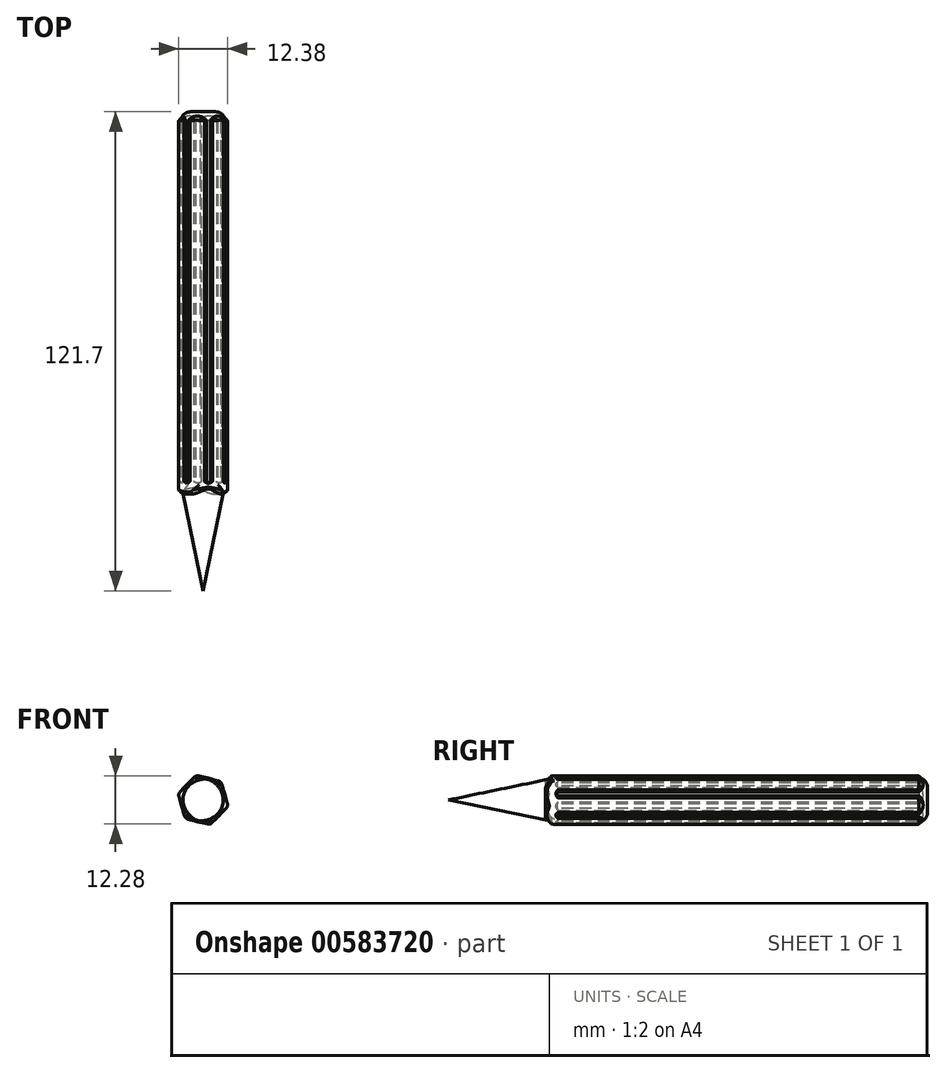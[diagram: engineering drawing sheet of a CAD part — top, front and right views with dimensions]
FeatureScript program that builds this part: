
annotation { "Feature Type Name" : "Feature", "Feature Type Description" : "" }
export const myFeature = defineFeature(function(context is Context, id is Id, definition is map)
    precondition{}
    {
        {
            var Q0;
            Q0=qCreatedBy(makeId("Right.planeOp"),FACE);
            var sketch = newSketch(context, id + "F0", { "sketchPlane" : qUnion([Q0])});
            skLineSegment(sketch, "E0.bottom", {"start": v(-45.04, 0) * mm, "end": v(49.08, 0) * mm});
            skLineSegment(sketch, "E0.top", {"start": v(-45.04, 5.71) * mm, "end": v(49.08, 5.71) * mm});
            skLineSegment(sketch, "E0.left", {"start": v(-45.04, 0) * mm, "end": v(-45.04, 5.71) * mm});
            skLineSegment(sketch, "E0.right", {"start": v(49.08, 0) * mm, "end": v(49.08, 5.71) * mm});
            skLineSegment(sketch, "E1", {"start": v(-45.04, 5.71) * mm, "end": v(-72.62, 0) * mm});
            skLineSegment(sketch, "E2", {"start": v(-72.62, 0) * mm, "end": v(-45.04, 0) * mm});
            skSolve(sketch);
        }
        {
            var Q0;
            Q0=qCreatedBy(makeId("Right.planeOp"),FACE);
            var sketch = newSketch(context, id + "F1", { "sketchPlane" : qUnion([Q0])});
            skSolve(sketch);
        }
        {
            var Q0;
            Q0 = qSketchRegion(id + "F1", true);
            var Q1;
            Q1=makeQuery(id+"F0.imprint","IMPRINT",FACE,{"disambiguationData":[TD([[makeQuery(id+"F0.imprint","IMPRINT",EDGE,{"derivedFrom":sQuery(id+"F0.wireOp",EDGE,"E0.left")}),1.0]])]});
            var Q2;
            Q2=makeQuery(id+"F0.imprint","IMPRINT",FACE,{"disambiguationData":[TD([[makeQuery(id+"F0.imprint","IMPRINT",EDGE,{"derivedFrom":sQuery(id+"F0.wireOp",EDGE,"E0.bottom")}),1.0]])]});
            var Q3;
            Q3=sQuery(id+"F0.wireOp",EDGE,"E0.bottom");
            revolve(context, id + "F2", {"entities" : qUnion([Q0, Q1, Q2]), "axis" : qUnion([Q3]), "revolveType" : RevolveType.FULL});
        }
        {
            var Q0;
            Q0=qCreatedBy(makeId("Front.planeOp"),FACE);
            var sketch = newSketch(context, id + "F3", { "sketchPlane" : qUnion([Q0])});
            skCircle(sketch, "E3.cCircle", {"center": v(0, 0) * mm, "radius": 5.66 * mm, "construction": true});
            skLineSegment(sketch, "E3.0", {"start": v(-4.53, -4.71) * mm, "end": v(-6.35, 1.57) * mm});
            skLineSegment(sketch, "E3.1", {"start": v(-6.35, 1.57) * mm, "end": v(-1.81, 6.28) * mm});
            skLineSegment(sketch, "E3.2", {"start": v(-1.81, 6.28) * mm, "end": v(4.53, 4.71) * mm});
            skLineSegment(sketch, "E3.3", {"start": v(4.53, 4.71) * mm, "end": v(6.35, -1.57) * mm});
            skLineSegment(sketch, "E3.4", {"start": v(6.35, -1.57) * mm, "end": v(1.81, -6.28) * mm});
            skLineSegment(sketch, "E3.5", {"start": v(1.81, -6.28) * mm, "end": v(-4.53, -4.71) * mm});
            skPoint(sketch, "E3.0.midPoint", {"position": v(-5.44, -1.57) * mm});
            skSolve(sketch);
        }
        {
            var Q0;
            Q0 = qSketchRegion(id + "F3", true);
            extrude(context, id + "F4", {"entities" : qUnion([Q0]), "operationType" : NewBodyOperationType.ADD, "endBound" : BoundingType.SYMMETRIC, "depth" : 93.98 * mm, "offsetDistance" : 25.4 * mm});
        }
        {
            var Q0;
            Q0=makeQuery(id+"F4.opExtrude","SWEPT_EDGE",EDGE,{"disambiguationData":[OSD([sQuery(id+"F3.wireOp",EDGE,"E3.3"),sQuery(id+"F3.wireOp",EDGE,"E3.4")])]});
            var Q1;
            Q1=makeQuery(id+"F4.opExtrude","SWEPT_EDGE",EDGE,{"disambiguationData":[OSD([sQuery(id+"F3.wireOp",EDGE,"E3.2"),sQuery(id+"F3.wireOp",EDGE,"E3.3")])]});
            var Q2;
            Q2=makeQuery(id+"F4.opExtrude","SWEPT_EDGE",EDGE,{"disambiguationData":[OSD([sQuery(id+"F3.wireOp",EDGE,"E3.1"),sQuery(id+"F3.wireOp",EDGE,"E3.2")])]});
            var Q3;
            Q3=makeQuery(id+"F4.opExtrude","SWEPT_EDGE",EDGE,{"disambiguationData":[OSD([sQuery(id+"F3.wireOp",EDGE,"E3.0"),sQuery(id+"F3.wireOp",EDGE,"E3.1")])]});
            var Q4;
            Q4=makeQuery(id+"F4.opExtrude","SWEPT_EDGE",EDGE,{"disambiguationData":[OSD([sQuery(id+"F3.wireOp",EDGE,"E3.0"),sQuery(id+"F3.wireOp",EDGE,"E3.5")])]});
            var Q5;
            Q5=makeQuery(id+"F4.opExtrude","SWEPT_EDGE",EDGE,{"disambiguationData":[OSD([sQuery(id+"F3.wireOp",EDGE,"E3.4"),sQuery(id+"F3.wireOp",EDGE,"E3.5")])]});
            var Q6;
            Q6=makeQuery(id+"F4.opExtrude","CAP_EDGE",EDGE,{"disambiguationData":[OSD([sQuery(id+"F3.wireOp",EDGE,"E3.5")])],"isStart":false});
            var Q7;
            Q7=makeQuery(id+"F4.opExtrude","CAP_EDGE",EDGE,{"disambiguationData":[OSD([sQuery(id+"F3.wireOp",EDGE,"E3.2")])],"isStart":false});
            fillet(context, id + "F5", {"entities" : qUnion([Q0, Q1, Q2, Q3, Q4, Q5, Q6, Q7]), "radius" : 1.27 * mm, "tangentPropagation" : true, "allowEdgeOverflow" : false});
        }
        {
            var Q0;
            Q0=makeQuery(id+"F2.opRevolve","SWEPT_EDGE",EDGE,{"disambiguationData":[OSD([sQuery(id+"F0.wireOp",EDGE,"E0.top"),sQuery(id+"F0.wireOp",EDGE,"E0.right")])]});
            fillet(context, id + "F6", {"entities" : qUnion([Q0]), "radius" : 2.54 * mm, "tangentPropagation" : true, "allowEdgeOverflow" : false});
        }
        {
            var Q0;
            {var subQ0=sQuery(id+"F3.wireOp",EDGE,"E3.0");var subQ1=sQuery(id+"F3.wireOp",EDGE,"E3.1");Q0=makeQuery(id+"F5.opFillet","BLEND_EDGE",EDGE,{"blendedFrom":[makeQuery(id+"F4.opExtrude","SWEPT_EDGE",EDGE,{"disambiguationData":[OSD([subQ0,subQ1])]}),makeQuery(id+"F4.boolean.opBoolean","SPLIT",FACE,{"disambiguationData":[TD([makeQuery(id+"F2.opRevolve","SWEPT_FACE",FACE,{"disambiguationData":[OSD([sQuery(id+"F0.wireOp",EDGE,"E0.top")])]}),makeQuery(id+"F4.opExtrude","SWEPT_FACE",FACE,{"disambiguationData":[OSD([subQ0])]}),makeQuery(id+"F4.opExtrude","SWEPT_FACE",FACE,{"disambiguationData":[OSD([subQ1])]})])],"derivedFrom":makeQuery(id+"F4.opExtrude","CAP_FACE",FACE,{"disambiguationData":[OSD([subQ0,subQ1,sQuery(id+"F3.wireOp",EDGE,"E3.2"),sQuery(id+"F3.wireOp",EDGE,"E3.3"),sQuery(id+"F3.wireOp",EDGE,"E3.4"),sQuery(id+"F3.wireOp",EDGE,"E3.5")])],"isStart":true})})],"blendedInto":[makeQuery(id+"F4.boolean.opBoolean","SPLIT",FACE,{"disambiguationData":[TD([makeQuery(id+"F2.opRevolve","SWEPT_FACE",FACE,{"disambiguationData":[OSD([sQuery(id+"F0.wireOp",EDGE,"E0.top")])]}),makeQuery(id+"F4.opExtrude","SWEPT_FACE",FACE,{"disambiguationData":[OSD([subQ0])]}),makeQuery(id+"F4.opExtrude","SWEPT_FACE",FACE,{"disambiguationData":[OSD([subQ1])]})])],"derivedFrom":makeQuery(id+"F4.opExtrude","CAP_FACE",FACE,{"disambiguationData":[OSD([subQ0,subQ1,sQuery(id+"F3.wireOp",EDGE,"E3.2"),sQuery(id+"F3.wireOp",EDGE,"E3.3"),sQuery(id+"F3.wireOp",EDGE,"E3.4"),sQuery(id+"F3.wireOp",EDGE,"E3.5")])],"isStart":true})})]});}
            var Q1;
            {var subQ0=sQuery(id+"F3.wireOp",EDGE,"E3.0");var subQ1=sQuery(id+"F3.wireOp",EDGE,"E3.1");Q1=makeQuery(id+"F4.boolean.opBoolean","SPLIT",EDGE,{"disambiguationData":[TD([makeQuery(id+"F4.opExtrude","SWEPT_FACE",FACE,{"disambiguationData":[OSD([subQ1])]})])],"derivedFrom":makeQuery(id+"F4.opExtrude","CAP_EDGE",EDGE,{"disambiguationData":[OSD([subQ0])],"isStart":true})});}
            var Q2;
            {var subQ0=sQuery(id+"F3.wireOp",EDGE,"E3.0");var subQ1=sQuery(id+"F3.wireOp",EDGE,"E3.1");Q2=makeQuery(id+"F4.boolean.opBoolean","SPLIT",EDGE,{"disambiguationData":[TD([makeQuery(id+"F4.opExtrude","SWEPT_FACE",FACE,{"disambiguationData":[OSD([subQ0])]})])],"derivedFrom":makeQuery(id+"F4.opExtrude","CAP_EDGE",EDGE,{"disambiguationData":[OSD([subQ1])],"isStart":true})});}
            var Q3;
            {var subQ0=sQuery(id+"F3.wireOp",EDGE,"E3.2");var subQ1=sQuery(id+"F3.wireOp",EDGE,"E3.1");Q3=makeQuery(id+"F4.boolean.opBoolean","SPLIT",EDGE,{"disambiguationData":[TD([makeQuery(id+"F4.opExtrude","SWEPT_FACE",FACE,{"disambiguationData":[OSD([subQ0])]})])],"derivedFrom":makeQuery(id+"F4.opExtrude","CAP_EDGE",EDGE,{"disambiguationData":[OSD([subQ1])],"isStart":true})});}
            var Q4;
            {var subQ0=sQuery(id+"F3.wireOp",EDGE,"E3.1");var subQ1=sQuery(id+"F3.wireOp",EDGE,"E3.2");Q4=makeQuery(id+"F5.opFillet","BLEND_EDGE",EDGE,{"blendedFrom":[makeQuery(id+"F4.opExtrude","SWEPT_EDGE",EDGE,{"disambiguationData":[OSD([subQ0,subQ1])]}),makeQuery(id+"F4.boolean.opBoolean","SPLIT",FACE,{"disambiguationData":[TD([makeQuery(id+"F2.opRevolve","SWEPT_FACE",FACE,{"disambiguationData":[OSD([sQuery(id+"F0.wireOp",EDGE,"E0.top")])]}),makeQuery(id+"F4.opExtrude","SWEPT_FACE",FACE,{"disambiguationData":[OSD([subQ0])]}),makeQuery(id+"F4.opExtrude","SWEPT_FACE",FACE,{"disambiguationData":[OSD([subQ1])]})])],"derivedFrom":makeQuery(id+"F4.opExtrude","CAP_FACE",FACE,{"disambiguationData":[OSD([sQuery(id+"F3.wireOp",EDGE,"E3.0"),subQ0,subQ1,sQuery(id+"F3.wireOp",EDGE,"E3.3"),sQuery(id+"F3.wireOp",EDGE,"E3.4"),sQuery(id+"F3.wireOp",EDGE,"E3.5")])],"isStart":true})})],"blendedInto":[makeQuery(id+"F4.boolean.opBoolean","SPLIT",FACE,{"disambiguationData":[TD([makeQuery(id+"F2.opRevolve","SWEPT_FACE",FACE,{"disambiguationData":[OSD([sQuery(id+"F0.wireOp",EDGE,"E0.top")])]}),makeQuery(id+"F4.opExtrude","SWEPT_FACE",FACE,{"disambiguationData":[OSD([subQ0])]}),makeQuery(id+"F4.opExtrude","SWEPT_FACE",FACE,{"disambiguationData":[OSD([subQ1])]})])],"derivedFrom":makeQuery(id+"F4.opExtrude","CAP_FACE",FACE,{"disambiguationData":[OSD([sQuery(id+"F3.wireOp",EDGE,"E3.0"),subQ0,subQ1,sQuery(id+"F3.wireOp",EDGE,"E3.3"),sQuery(id+"F3.wireOp",EDGE,"E3.4"),sQuery(id+"F3.wireOp",EDGE,"E3.5")])],"isStart":true})})]});}
            var Q5;
            {var subQ0=sQuery(id+"F3.wireOp",EDGE,"E3.2");var subQ1=sQuery(id+"F3.wireOp",EDGE,"E3.1");Q5=makeQuery(id+"F4.boolean.opBoolean","SPLIT",EDGE,{"disambiguationData":[TD([makeQuery(id+"F4.opExtrude","SWEPT_FACE",FACE,{"disambiguationData":[OSD([subQ1])]})])],"derivedFrom":makeQuery(id+"F4.opExtrude","CAP_EDGE",EDGE,{"disambiguationData":[OSD([subQ0])],"isStart":true})});}
            var Q6;
            {var subQ0=sQuery(id+"F3.wireOp",EDGE,"E3.3");var subQ1=sQuery(id+"F3.wireOp",EDGE,"E3.2");Q6=makeQuery(id+"F4.boolean.opBoolean","SPLIT",EDGE,{"disambiguationData":[TD([makeQuery(id+"F4.opExtrude","SWEPT_FACE",FACE,{"disambiguationData":[OSD([subQ0])]})])],"derivedFrom":makeQuery(id+"F4.opExtrude","CAP_EDGE",EDGE,{"disambiguationData":[OSD([subQ1])],"isStart":true})});}
            var Q7;
            {var subQ0=sQuery(id+"F3.wireOp",EDGE,"E3.3");var subQ1=sQuery(id+"F3.wireOp",EDGE,"E3.2");Q7=makeQuery(id+"F5.opFillet","BLEND_EDGE",EDGE,{"blendedFrom":[makeQuery(id+"F4.opExtrude","SWEPT_EDGE",EDGE,{"disambiguationData":[OSD([subQ1,subQ0])]}),makeQuery(id+"F4.boolean.opBoolean","SPLIT",FACE,{"disambiguationData":[TD([makeQuery(id+"F2.opRevolve","SWEPT_FACE",FACE,{"disambiguationData":[OSD([sQuery(id+"F0.wireOp",EDGE,"E0.top")])]}),makeQuery(id+"F4.opExtrude","SWEPT_FACE",FACE,{"disambiguationData":[OSD([subQ1])]}),makeQuery(id+"F4.opExtrude","SWEPT_FACE",FACE,{"disambiguationData":[OSD([subQ0])]})])],"derivedFrom":makeQuery(id+"F4.opExtrude","CAP_FACE",FACE,{"disambiguationData":[OSD([sQuery(id+"F3.wireOp",EDGE,"E3.0"),sQuery(id+"F3.wireOp",EDGE,"E3.1"),subQ1,subQ0,sQuery(id+"F3.wireOp",EDGE,"E3.4"),sQuery(id+"F3.wireOp",EDGE,"E3.5")])],"isStart":true})})],"blendedInto":[makeQuery(id+"F4.boolean.opBoolean","SPLIT",FACE,{"disambiguationData":[TD([makeQuery(id+"F2.opRevolve","SWEPT_FACE",FACE,{"disambiguationData":[OSD([sQuery(id+"F0.wireOp",EDGE,"E0.top")])]}),makeQuery(id+"F4.opExtrude","SWEPT_FACE",FACE,{"disambiguationData":[OSD([subQ1])]}),makeQuery(id+"F4.opExtrude","SWEPT_FACE",FACE,{"disambiguationData":[OSD([subQ0])]})])],"derivedFrom":makeQuery(id+"F4.opExtrude","CAP_FACE",FACE,{"disambiguationData":[OSD([sQuery(id+"F3.wireOp",EDGE,"E3.0"),sQuery(id+"F3.wireOp",EDGE,"E3.1"),subQ1,subQ0,sQuery(id+"F3.wireOp",EDGE,"E3.4"),sQuery(id+"F3.wireOp",EDGE,"E3.5")])],"isStart":true})})]});}
            var Q8;
            {var subQ0=sQuery(id+"F3.wireOp",EDGE,"E3.3");var subQ1=sQuery(id+"F3.wireOp",EDGE,"E3.2");Q8=makeQuery(id+"F4.boolean.opBoolean","SPLIT",EDGE,{"disambiguationData":[TD([makeQuery(id+"F4.opExtrude","SWEPT_FACE",FACE,{"disambiguationData":[OSD([subQ1])]})])],"derivedFrom":makeQuery(id+"F4.opExtrude","CAP_EDGE",EDGE,{"disambiguationData":[OSD([subQ0])],"isStart":true})});}
            var Q9;
            {var subQ0=sQuery(id+"F3.wireOp",EDGE,"E3.3");var subQ1=sQuery(id+"F3.wireOp",EDGE,"E3.4");Q9=makeQuery(id+"F4.boolean.opBoolean","SPLIT",EDGE,{"disambiguationData":[TD([makeQuery(id+"F4.opExtrude","SWEPT_FACE",FACE,{"disambiguationData":[OSD([subQ1])]})])],"derivedFrom":makeQuery(id+"F4.opExtrude","CAP_EDGE",EDGE,{"disambiguationData":[OSD([subQ0])],"isStart":true})});}
            var Q10;
            {var subQ0=sQuery(id+"F3.wireOp",EDGE,"E3.3");var subQ1=sQuery(id+"F3.wireOp",EDGE,"E3.4");Q10=makeQuery(id+"F5.opFillet","BLEND_EDGE",EDGE,{"blendedFrom":[makeQuery(id+"F4.opExtrude","SWEPT_EDGE",EDGE,{"disambiguationData":[OSD([subQ0,subQ1])]}),makeQuery(id+"F4.boolean.opBoolean","SPLIT",FACE,{"disambiguationData":[TD([makeQuery(id+"F2.opRevolve","SWEPT_FACE",FACE,{"disambiguationData":[OSD([sQuery(id+"F0.wireOp",EDGE,"E0.top")])]}),makeQuery(id+"F4.opExtrude","SWEPT_FACE",FACE,{"disambiguationData":[OSD([subQ0])]}),makeQuery(id+"F4.opExtrude","SWEPT_FACE",FACE,{"disambiguationData":[OSD([subQ1])]})])],"derivedFrom":makeQuery(id+"F4.opExtrude","CAP_FACE",FACE,{"disambiguationData":[OSD([sQuery(id+"F3.wireOp",EDGE,"E3.0"),sQuery(id+"F3.wireOp",EDGE,"E3.1"),sQuery(id+"F3.wireOp",EDGE,"E3.2"),subQ0,subQ1,sQuery(id+"F3.wireOp",EDGE,"E3.5")])],"isStart":true})})],"blendedInto":[makeQuery(id+"F4.boolean.opBoolean","SPLIT",FACE,{"disambiguationData":[TD([makeQuery(id+"F2.opRevolve","SWEPT_FACE",FACE,{"disambiguationData":[OSD([sQuery(id+"F0.wireOp",EDGE,"E0.top")])]}),makeQuery(id+"F4.opExtrude","SWEPT_FACE",FACE,{"disambiguationData":[OSD([subQ0])]}),makeQuery(id+"F4.opExtrude","SWEPT_FACE",FACE,{"disambiguationData":[OSD([subQ1])]})])],"derivedFrom":makeQuery(id+"F4.opExtrude","CAP_FACE",FACE,{"disambiguationData":[OSD([sQuery(id+"F3.wireOp",EDGE,"E3.0"),sQuery(id+"F3.wireOp",EDGE,"E3.1"),sQuery(id+"F3.wireOp",EDGE,"E3.2"),subQ0,subQ1,sQuery(id+"F3.wireOp",EDGE,"E3.5")])],"isStart":true})})]});}
            var Q11;
            {var subQ0=sQuery(id+"F3.wireOp",EDGE,"E3.3");var subQ1=sQuery(id+"F3.wireOp",EDGE,"E3.4");Q11=makeQuery(id+"F4.boolean.opBoolean","SPLIT",EDGE,{"disambiguationData":[TD([makeQuery(id+"F4.opExtrude","SWEPT_FACE",FACE,{"disambiguationData":[OSD([subQ0])]})])],"derivedFrom":makeQuery(id+"F4.opExtrude","CAP_EDGE",EDGE,{"disambiguationData":[OSD([subQ1])],"isStart":true})});}
            var Q12;
            {var subQ0=sQuery(id+"F3.wireOp",EDGE,"E3.5");var subQ1=sQuery(id+"F3.wireOp",EDGE,"E3.4");Q12=makeQuery(id+"F4.boolean.opBoolean","SPLIT",EDGE,{"disambiguationData":[TD([makeQuery(id+"F4.opExtrude","SWEPT_FACE",FACE,{"disambiguationData":[OSD([subQ0])]})])],"derivedFrom":makeQuery(id+"F4.opExtrude","CAP_EDGE",EDGE,{"disambiguationData":[OSD([subQ1])],"isStart":true})});}
            var Q13;
            {var subQ0=sQuery(id+"F3.wireOp",EDGE,"E3.4");var subQ1=sQuery(id+"F3.wireOp",EDGE,"E3.5");Q13=makeQuery(id+"F5.opFillet","BLEND_EDGE",EDGE,{"blendedFrom":[makeQuery(id+"F4.opExtrude","SWEPT_EDGE",EDGE,{"disambiguationData":[OSD([subQ0,subQ1])]}),makeQuery(id+"F4.boolean.opBoolean","SPLIT",FACE,{"disambiguationData":[TD([makeQuery(id+"F2.opRevolve","SWEPT_FACE",FACE,{"disambiguationData":[OSD([sQuery(id+"F0.wireOp",EDGE,"E0.top")])]}),makeQuery(id+"F4.opExtrude","SWEPT_FACE",FACE,{"disambiguationData":[OSD([subQ0])]}),makeQuery(id+"F4.opExtrude","SWEPT_FACE",FACE,{"disambiguationData":[OSD([subQ1])]})])],"derivedFrom":makeQuery(id+"F4.opExtrude","CAP_FACE",FACE,{"disambiguationData":[OSD([sQuery(id+"F3.wireOp",EDGE,"E3.0"),sQuery(id+"F3.wireOp",EDGE,"E3.1"),sQuery(id+"F3.wireOp",EDGE,"E3.2"),sQuery(id+"F3.wireOp",EDGE,"E3.3"),subQ0,subQ1])],"isStart":true})})],"blendedInto":[makeQuery(id+"F4.boolean.opBoolean","SPLIT",FACE,{"disambiguationData":[TD([makeQuery(id+"F2.opRevolve","SWEPT_FACE",FACE,{"disambiguationData":[OSD([sQuery(id+"F0.wireOp",EDGE,"E0.top")])]}),makeQuery(id+"F4.opExtrude","SWEPT_FACE",FACE,{"disambiguationData":[OSD([subQ0])]}),makeQuery(id+"F4.opExtrude","SWEPT_FACE",FACE,{"disambiguationData":[OSD([subQ1])]})])],"derivedFrom":makeQuery(id+"F4.opExtrude","CAP_FACE",FACE,{"disambiguationData":[OSD([sQuery(id+"F3.wireOp",EDGE,"E3.0"),sQuery(id+"F3.wireOp",EDGE,"E3.1"),sQuery(id+"F3.wireOp",EDGE,"E3.2"),sQuery(id+"F3.wireOp",EDGE,"E3.3"),subQ0,subQ1])],"isStart":true})})]});}
            var Q14;
            {var subQ0=sQuery(id+"F3.wireOp",EDGE,"E3.5");var subQ1=sQuery(id+"F3.wireOp",EDGE,"E3.4");Q14=makeQuery(id+"F4.boolean.opBoolean","SPLIT",EDGE,{"disambiguationData":[TD([makeQuery(id+"F4.opExtrude","SWEPT_FACE",FACE,{"disambiguationData":[OSD([subQ1])]})])],"derivedFrom":makeQuery(id+"F4.opExtrude","CAP_EDGE",EDGE,{"disambiguationData":[OSD([subQ0])],"isStart":true})});}
            var Q15;
            {var subQ0=sQuery(id+"F3.wireOp",EDGE,"E3.0");var subQ1=sQuery(id+"F3.wireOp",EDGE,"E3.5");Q15=makeQuery(id+"F4.boolean.opBoolean","SPLIT",EDGE,{"disambiguationData":[TD([makeQuery(id+"F4.opExtrude","SWEPT_FACE",FACE,{"disambiguationData":[OSD([subQ0])]})])],"derivedFrom":makeQuery(id+"F4.opExtrude","CAP_EDGE",EDGE,{"disambiguationData":[OSD([subQ1])],"isStart":true})});}
            var Q16;
            {var subQ0=sQuery(id+"F3.wireOp",EDGE,"E3.0");var subQ1=sQuery(id+"F3.wireOp",EDGE,"E3.5");Q16=makeQuery(id+"F5.opFillet","BLEND_EDGE",EDGE,{"blendedFrom":[makeQuery(id+"F4.opExtrude","SWEPT_EDGE",EDGE,{"disambiguationData":[OSD([subQ0,subQ1])]}),makeQuery(id+"F4.boolean.opBoolean","SPLIT",FACE,{"disambiguationData":[TD([makeQuery(id+"F2.opRevolve","SWEPT_FACE",FACE,{"disambiguationData":[OSD([sQuery(id+"F0.wireOp",EDGE,"E0.top")])]}),makeQuery(id+"F4.opExtrude","SWEPT_FACE",FACE,{"disambiguationData":[OSD([subQ0])]}),makeQuery(id+"F4.opExtrude","SWEPT_FACE",FACE,{"disambiguationData":[OSD([subQ1])]})])],"derivedFrom":makeQuery(id+"F4.opExtrude","CAP_FACE",FACE,{"disambiguationData":[OSD([subQ0,sQuery(id+"F3.wireOp",EDGE,"E3.1"),sQuery(id+"F3.wireOp",EDGE,"E3.2"),sQuery(id+"F3.wireOp",EDGE,"E3.3"),sQuery(id+"F3.wireOp",EDGE,"E3.4"),subQ1])],"isStart":true})})],"blendedInto":[makeQuery(id+"F4.boolean.opBoolean","SPLIT",FACE,{"disambiguationData":[TD([makeQuery(id+"F2.opRevolve","SWEPT_FACE",FACE,{"disambiguationData":[OSD([sQuery(id+"F0.wireOp",EDGE,"E0.top")])]}),makeQuery(id+"F4.opExtrude","SWEPT_FACE",FACE,{"disambiguationData":[OSD([subQ0])]}),makeQuery(id+"F4.opExtrude","SWEPT_FACE",FACE,{"disambiguationData":[OSD([subQ1])]})])],"derivedFrom":makeQuery(id+"F4.opExtrude","CAP_FACE",FACE,{"disambiguationData":[OSD([subQ0,sQuery(id+"F3.wireOp",EDGE,"E3.1"),sQuery(id+"F3.wireOp",EDGE,"E3.2"),sQuery(id+"F3.wireOp",EDGE,"E3.3"),sQuery(id+"F3.wireOp",EDGE,"E3.4"),subQ1])],"isStart":true})})]});}
            var Q17;
            {var subQ0=sQuery(id+"F3.wireOp",EDGE,"E3.0");var subQ1=sQuery(id+"F3.wireOp",EDGE,"E3.5");Q17=makeQuery(id+"F4.boolean.opBoolean","SPLIT",EDGE,{"disambiguationData":[TD([makeQuery(id+"F4.opExtrude","SWEPT_FACE",FACE,{"disambiguationData":[OSD([subQ1])]})])],"derivedFrom":makeQuery(id+"F4.opExtrude","CAP_EDGE",EDGE,{"disambiguationData":[OSD([subQ0])],"isStart":true})});}
            fillet(context, id + "F7", {"entities" : qUnion([Q0, Q1, Q2, Q3, Q4, Q5, Q6, Q7, Q8, Q9, Q10, Q11, Q12, Q13, Q14, Q15, Q16, Q17]), "radius" : 0.25 * mm, "tangentPropagation" : true, "allowEdgeOverflow" : false});
        }
        {
            var Q0;
            {var subQ0=sQuery(id+"F0.wireOp",EDGE,"E0.top");var subQ1=sQuery(id+"F3.wireOp",EDGE,"E3.0");var subQ2=sQuery(id+"F3.wireOp",EDGE,"E3.1");Q0=makeQuery(id+"F7.opFillet","BLEND_EDGE",EDGE,{"blendedFrom":[makeQuery(id+"F4.boolean.opBoolean","SPLIT",EDGE,{"disambiguationData":[TD([makeQuery(id+"F4.opExtrude","SWEPT_FACE",FACE,{"disambiguationData":[OSD([subQ2])]})])],"derivedFrom":makeQuery(id+"F4.opExtrude","CAP_EDGE",EDGE,{"disambiguationData":[OSD([subQ1])],"isStart":true})}),makeQuery(id+"F6.opFillet","BLEND_FACE",FACE,{"disambiguationData":[OSD([subQ0,sQuery(id+"F0.wireOp",EDGE,"E0.right")])]})],"blendedInto":[makeQuery(id+"F6.opFillet","BLEND_FACE",FACE,{"disambiguationData":[OSD([subQ0,sQuery(id+"F0.wireOp",EDGE,"E0.right")])]})]});}
            var Q1;
            {var subQ0=sQuery(id+"F0.wireOp",EDGE,"E0.top");var subQ1=sQuery(id+"F3.wireOp",EDGE,"E3.0");var subQ2=sQuery(id+"F3.wireOp",EDGE,"E3.1");Q1=makeQuery(id+"F7.opFillet","BLEND_EDGE",EDGE,{"blendedFrom":[makeQuery(id+"F4.boolean.opBoolean","SPLIT",EDGE,{"disambiguationData":[TD([makeQuery(id+"F4.opExtrude","SWEPT_FACE",FACE,{"disambiguationData":[OSD([subQ1])]})])],"derivedFrom":makeQuery(id+"F4.opExtrude","CAP_EDGE",EDGE,{"disambiguationData":[OSD([subQ2])],"isStart":true})}),makeQuery(id+"F6.opFillet","BLEND_FACE",FACE,{"disambiguationData":[OSD([subQ0,sQuery(id+"F0.wireOp",EDGE,"E0.right")])]})],"blendedInto":[makeQuery(id+"F6.opFillet","BLEND_FACE",FACE,{"disambiguationData":[OSD([subQ0,sQuery(id+"F0.wireOp",EDGE,"E0.right")])]})]});}
            chamfer(context, id + "F8", {"entities" : qUnion([Q0, Q1]), "width" : 5.08 * mm, "tangentPropagation" : true});
        }
        {
            var Q0;
            {var subQ0=sQuery(id+"F0.wireOp",EDGE,"E0.top");var subQ1=sQuery(id+"F3.wireOp",EDGE,"E3.0");var subQ2=sQuery(id+"F3.wireOp",EDGE,"E3.5");Q0=makeQuery(id+"F7.opFillet","BLEND_EDGE",EDGE,{"blendedFrom":[makeQuery(id+"F4.boolean.opBoolean","SPLIT",EDGE,{"disambiguationData":[TD([makeQuery(id+"F4.opExtrude","SWEPT_FACE",FACE,{"disambiguationData":[OSD([subQ2])]})])],"derivedFrom":makeQuery(id+"F4.opExtrude","CAP_EDGE",EDGE,{"disambiguationData":[OSD([subQ1])],"isStart":true})}),makeQuery(id+"F6.opFillet","BLEND_FACE",FACE,{"disambiguationData":[OSD([subQ0,sQuery(id+"F0.wireOp",EDGE,"E0.right")])]})],"blendedInto":[makeQuery(id+"F6.opFillet","BLEND_FACE",FACE,{"disambiguationData":[OSD([subQ0,sQuery(id+"F0.wireOp",EDGE,"E0.right")])]})]});}
            var Q1;
            {var subQ0=sQuery(id+"F0.wireOp",EDGE,"E0.top");var subQ1=sQuery(id+"F3.wireOp",EDGE,"E3.0");var subQ2=sQuery(id+"F3.wireOp",EDGE,"E3.5");Q1=makeQuery(id+"F7.opFillet","BLEND_EDGE",EDGE,{"blendedFrom":[makeQuery(id+"F4.boolean.opBoolean","SPLIT",EDGE,{"disambiguationData":[TD([makeQuery(id+"F4.opExtrude","SWEPT_FACE",FACE,{"disambiguationData":[OSD([subQ1])]})])],"derivedFrom":makeQuery(id+"F4.opExtrude","CAP_EDGE",EDGE,{"disambiguationData":[OSD([subQ2])],"isStart":true})}),makeQuery(id+"F6.opFillet","BLEND_FACE",FACE,{"disambiguationData":[OSD([subQ0,sQuery(id+"F0.wireOp",EDGE,"E0.right")])]})],"blendedInto":[makeQuery(id+"F6.opFillet","BLEND_FACE",FACE,{"disambiguationData":[OSD([subQ0,sQuery(id+"F0.wireOp",EDGE,"E0.right")])]})]});}
            chamfer(context, id + "F9", {"entities" : qUnion([Q0, Q1]), "width" : 5.08 * mm, "tangentPropagation" : true});
        }
        {
            var Q0;
            {var subQ0=sQuery(id+"F0.wireOp",EDGE,"E0.top");var subQ1=sQuery(id+"F3.wireOp",EDGE,"E3.5");var subQ2=sQuery(id+"F3.wireOp",EDGE,"E3.4");Q0=makeQuery(id+"F7.opFillet","BLEND_EDGE",EDGE,{"blendedFrom":[makeQuery(id+"F4.boolean.opBoolean","SPLIT",EDGE,{"disambiguationData":[TD([makeQuery(id+"F4.opExtrude","SWEPT_FACE",FACE,{"disambiguationData":[OSD([subQ2])]})])],"derivedFrom":makeQuery(id+"F4.opExtrude","CAP_EDGE",EDGE,{"disambiguationData":[OSD([subQ1])],"isStart":true})}),makeQuery(id+"F6.opFillet","BLEND_FACE",FACE,{"disambiguationData":[OSD([subQ0,sQuery(id+"F0.wireOp",EDGE,"E0.right")])]})],"blendedInto":[makeQuery(id+"F6.opFillet","BLEND_FACE",FACE,{"disambiguationData":[OSD([subQ0,sQuery(id+"F0.wireOp",EDGE,"E0.right")])]})]});}
            var Q1;
            {var subQ0=sQuery(id+"F0.wireOp",EDGE,"E0.top");var subQ1=sQuery(id+"F3.wireOp",EDGE,"E3.5");var subQ2=sQuery(id+"F3.wireOp",EDGE,"E3.4");Q1=makeQuery(id+"F7.opFillet","BLEND_EDGE",EDGE,{"blendedFrom":[makeQuery(id+"F4.boolean.opBoolean","SPLIT",EDGE,{"disambiguationData":[TD([makeQuery(id+"F4.opExtrude","SWEPT_FACE",FACE,{"disambiguationData":[OSD([subQ1])]})])],"derivedFrom":makeQuery(id+"F4.opExtrude","CAP_EDGE",EDGE,{"disambiguationData":[OSD([subQ2])],"isStart":true})}),makeQuery(id+"F6.opFillet","BLEND_FACE",FACE,{"disambiguationData":[OSD([subQ0,sQuery(id+"F0.wireOp",EDGE,"E0.right")])]})],"blendedInto":[makeQuery(id+"F6.opFillet","BLEND_FACE",FACE,{"disambiguationData":[OSD([subQ0,sQuery(id+"F0.wireOp",EDGE,"E0.right")])]})]});}
            var Q2;
            {var subQ0=sQuery(id+"F0.wireOp",EDGE,"E0.top");var subQ1=sQuery(id+"F3.wireOp",EDGE,"E3.4");var subQ2=sQuery(id+"F3.wireOp",EDGE,"E3.5");Q2=makeQuery(id+"F6.opFillet","BLEND_EDGE",EDGE,{"blendedFrom":[makeQuery(id+"F2.opRevolve","SWEPT_EDGE",EDGE,{"disambiguationData":[OSD([subQ0,sQuery(id+"F0.wireOp",EDGE,"E0.right")])]}),makeQuery(id+"F4.boolean.opBoolean","SPLIT",FACE,{"disambiguationData":[TD([makeQuery(id+"F2.opRevolve","SWEPT_FACE",FACE,{"disambiguationData":[OSD([subQ0])]}),makeQuery(id+"F4.opExtrude","SWEPT_FACE",FACE,{"disambiguationData":[OSD([subQ1])]}),makeQuery(id+"F4.opExtrude","SWEPT_FACE",FACE,{"disambiguationData":[OSD([subQ2])]})])],"derivedFrom":makeQuery(id+"F4.opExtrude","CAP_FACE",FACE,{"disambiguationData":[OSD([sQuery(id+"F3.wireOp",EDGE,"E3.0"),sQuery(id+"F3.wireOp",EDGE,"E3.1"),sQuery(id+"F3.wireOp",EDGE,"E3.2"),sQuery(id+"F3.wireOp",EDGE,"E3.3"),subQ1,subQ2])],"isStart":true})})],"blendedInto":[makeQuery(id+"F4.boolean.opBoolean","SPLIT",FACE,{"disambiguationData":[TD([makeQuery(id+"F2.opRevolve","SWEPT_FACE",FACE,{"disambiguationData":[OSD([subQ0])]}),makeQuery(id+"F4.opExtrude","SWEPT_FACE",FACE,{"disambiguationData":[OSD([subQ1])]}),makeQuery(id+"F4.opExtrude","SWEPT_FACE",FACE,{"disambiguationData":[OSD([subQ2])]})])],"derivedFrom":makeQuery(id+"F4.opExtrude","CAP_FACE",FACE,{"disambiguationData":[OSD([sQuery(id+"F3.wireOp",EDGE,"E3.0"),sQuery(id+"F3.wireOp",EDGE,"E3.1"),sQuery(id+"F3.wireOp",EDGE,"E3.2"),sQuery(id+"F3.wireOp",EDGE,"E3.3"),subQ1,subQ2])],"isStart":true})})]});}
            chamfer(context, id + "F10", {"entities" : qUnion([Q0, Q1, Q2]), "width" : 5.08 * mm, "tangentPropagation" : true});
        }
        {
            var Q0;
            {var subQ0=sQuery(id+"F0.wireOp",EDGE,"E0.top");var subQ1=sQuery(id+"F3.wireOp",EDGE,"E3.3");var subQ2=sQuery(id+"F3.wireOp",EDGE,"E3.4");Q0=makeQuery(id+"F6.opFillet","BLEND_EDGE",EDGE,{"blendedFrom":[makeQuery(id+"F2.opRevolve","SWEPT_EDGE",EDGE,{"disambiguationData":[OSD([subQ0,sQuery(id+"F0.wireOp",EDGE,"E0.right")])]}),makeQuery(id+"F4.boolean.opBoolean","SPLIT",FACE,{"disambiguationData":[TD([makeQuery(id+"F2.opRevolve","SWEPT_FACE",FACE,{"disambiguationData":[OSD([subQ0])]}),makeQuery(id+"F4.opExtrude","SWEPT_FACE",FACE,{"disambiguationData":[OSD([subQ1])]}),makeQuery(id+"F4.opExtrude","SWEPT_FACE",FACE,{"disambiguationData":[OSD([subQ2])]})])],"derivedFrom":makeQuery(id+"F4.opExtrude","CAP_FACE",FACE,{"disambiguationData":[OSD([sQuery(id+"F3.wireOp",EDGE,"E3.0"),sQuery(id+"F3.wireOp",EDGE,"E3.1"),sQuery(id+"F3.wireOp",EDGE,"E3.2"),subQ1,subQ2,sQuery(id+"F3.wireOp",EDGE,"E3.5")])],"isStart":true})})],"blendedInto":[makeQuery(id+"F4.boolean.opBoolean","SPLIT",FACE,{"disambiguationData":[TD([makeQuery(id+"F2.opRevolve","SWEPT_FACE",FACE,{"disambiguationData":[OSD([subQ0])]}),makeQuery(id+"F4.opExtrude","SWEPT_FACE",FACE,{"disambiguationData":[OSD([subQ1])]}),makeQuery(id+"F4.opExtrude","SWEPT_FACE",FACE,{"disambiguationData":[OSD([subQ2])]})])],"derivedFrom":makeQuery(id+"F4.opExtrude","CAP_FACE",FACE,{"disambiguationData":[OSD([sQuery(id+"F3.wireOp",EDGE,"E3.0"),sQuery(id+"F3.wireOp",EDGE,"E3.1"),sQuery(id+"F3.wireOp",EDGE,"E3.2"),subQ1,subQ2,sQuery(id+"F3.wireOp",EDGE,"E3.5")])],"isStart":true})})]});}
            var Q1;
            {var subQ0=sQuery(id+"F0.wireOp",EDGE,"E0.top");var subQ1=sQuery(id+"F3.wireOp",EDGE,"E3.3");var subQ2=sQuery(id+"F3.wireOp",EDGE,"E3.4");Q1=makeQuery(id+"F7.opFillet","BLEND_EDGE",EDGE,{"blendedFrom":[makeQuery(id+"F4.boolean.opBoolean","SPLIT",EDGE,{"disambiguationData":[TD([makeQuery(id+"F4.opExtrude","SWEPT_FACE",FACE,{"disambiguationData":[OSD([subQ1])]})])],"derivedFrom":makeQuery(id+"F4.opExtrude","CAP_EDGE",EDGE,{"disambiguationData":[OSD([subQ2])],"isStart":true})}),makeQuery(id+"F6.opFillet","BLEND_FACE",FACE,{"disambiguationData":[OSD([subQ0,sQuery(id+"F0.wireOp",EDGE,"E0.right")])]})],"blendedInto":[makeQuery(id+"F6.opFillet","BLEND_FACE",FACE,{"disambiguationData":[OSD([subQ0,sQuery(id+"F0.wireOp",EDGE,"E0.right")])]})]});}
            var Q2;
            {var subQ0=sQuery(id+"F0.wireOp",EDGE,"E0.top");var subQ1=sQuery(id+"F3.wireOp",EDGE,"E3.3");var subQ2=sQuery(id+"F3.wireOp",EDGE,"E3.4");Q2=makeQuery(id+"F7.opFillet","BLEND_EDGE",EDGE,{"blendedFrom":[makeQuery(id+"F4.boolean.opBoolean","SPLIT",EDGE,{"disambiguationData":[TD([makeQuery(id+"F4.opExtrude","SWEPT_FACE",FACE,{"disambiguationData":[OSD([subQ2])]})])],"derivedFrom":makeQuery(id+"F4.opExtrude","CAP_EDGE",EDGE,{"disambiguationData":[OSD([subQ1])],"isStart":true})}),makeQuery(id+"F6.opFillet","BLEND_FACE",FACE,{"disambiguationData":[OSD([subQ0,sQuery(id+"F0.wireOp",EDGE,"E0.right")])]})],"blendedInto":[makeQuery(id+"F6.opFillet","BLEND_FACE",FACE,{"disambiguationData":[OSD([subQ0,sQuery(id+"F0.wireOp",EDGE,"E0.right")])]})]});}
            chamfer(context, id + "F11", {"entities" : qUnion([Q0, Q1, Q2]), "width" : 5.08 * mm, "tangentPropagation" : true});
        }
        {
            var Q0;
            {var subQ0=sQuery(id+"F0.wireOp",EDGE,"E0.top");var subQ1=sQuery(id+"F3.wireOp",EDGE,"E3.3");var subQ2=sQuery(id+"F3.wireOp",EDGE,"E3.2");Q0=makeQuery(id+"F7.opFillet","BLEND_EDGE",EDGE,{"blendedFrom":[makeQuery(id+"F4.boolean.opBoolean","SPLIT",EDGE,{"disambiguationData":[TD([makeQuery(id+"F4.opExtrude","SWEPT_FACE",FACE,{"disambiguationData":[OSD([subQ2])]})])],"derivedFrom":makeQuery(id+"F4.opExtrude","CAP_EDGE",EDGE,{"disambiguationData":[OSD([subQ1])],"isStart":true})}),makeQuery(id+"F6.opFillet","BLEND_FACE",FACE,{"disambiguationData":[OSD([subQ0,sQuery(id+"F0.wireOp",EDGE,"E0.right")])]})],"blendedInto":[makeQuery(id+"F6.opFillet","BLEND_FACE",FACE,{"disambiguationData":[OSD([subQ0,sQuery(id+"F0.wireOp",EDGE,"E0.right")])]})]});}
            var Q1;
            {var subQ0=sQuery(id+"F0.wireOp",EDGE,"E0.top");var subQ1=sQuery(id+"F3.wireOp",EDGE,"E3.3");var subQ2=sQuery(id+"F3.wireOp",EDGE,"E3.2");Q1=makeQuery(id+"F6.opFillet","BLEND_EDGE",EDGE,{"blendedFrom":[makeQuery(id+"F2.opRevolve","SWEPT_EDGE",EDGE,{"disambiguationData":[OSD([subQ0,sQuery(id+"F0.wireOp",EDGE,"E0.right")])]}),makeQuery(id+"F4.boolean.opBoolean","SPLIT",FACE,{"disambiguationData":[TD([makeQuery(id+"F2.opRevolve","SWEPT_FACE",FACE,{"disambiguationData":[OSD([subQ0])]}),makeQuery(id+"F4.opExtrude","SWEPT_FACE",FACE,{"disambiguationData":[OSD([subQ2])]}),makeQuery(id+"F4.opExtrude","SWEPT_FACE",FACE,{"disambiguationData":[OSD([subQ1])]})])],"derivedFrom":makeQuery(id+"F4.opExtrude","CAP_FACE",FACE,{"disambiguationData":[OSD([sQuery(id+"F3.wireOp",EDGE,"E3.0"),sQuery(id+"F3.wireOp",EDGE,"E3.1"),subQ2,subQ1,sQuery(id+"F3.wireOp",EDGE,"E3.4"),sQuery(id+"F3.wireOp",EDGE,"E3.5")])],"isStart":true})})],"blendedInto":[makeQuery(id+"F4.boolean.opBoolean","SPLIT",FACE,{"disambiguationData":[TD([makeQuery(id+"F2.opRevolve","SWEPT_FACE",FACE,{"disambiguationData":[OSD([subQ0])]}),makeQuery(id+"F4.opExtrude","SWEPT_FACE",FACE,{"disambiguationData":[OSD([subQ2])]}),makeQuery(id+"F4.opExtrude","SWEPT_FACE",FACE,{"disambiguationData":[OSD([subQ1])]})])],"derivedFrom":makeQuery(id+"F4.opExtrude","CAP_FACE",FACE,{"disambiguationData":[OSD([sQuery(id+"F3.wireOp",EDGE,"E3.0"),sQuery(id+"F3.wireOp",EDGE,"E3.1"),subQ2,subQ1,sQuery(id+"F3.wireOp",EDGE,"E3.4"),sQuery(id+"F3.wireOp",EDGE,"E3.5")])],"isStart":true})})]});}
            var Q2;
            {var subQ0=sQuery(id+"F0.wireOp",EDGE,"E0.top");var subQ1=sQuery(id+"F3.wireOp",EDGE,"E3.3");var subQ2=sQuery(id+"F3.wireOp",EDGE,"E3.2");Q2=makeQuery(id+"F7.opFillet","BLEND_EDGE",EDGE,{"blendedFrom":[makeQuery(id+"F4.boolean.opBoolean","SPLIT",EDGE,{"disambiguationData":[TD([makeQuery(id+"F4.opExtrude","SWEPT_FACE",FACE,{"disambiguationData":[OSD([subQ1])]})])],"derivedFrom":makeQuery(id+"F4.opExtrude","CAP_EDGE",EDGE,{"disambiguationData":[OSD([subQ2])],"isStart":true})}),makeQuery(id+"F6.opFillet","BLEND_FACE",FACE,{"disambiguationData":[OSD([subQ0,sQuery(id+"F0.wireOp",EDGE,"E0.right")])]})],"blendedInto":[makeQuery(id+"F6.opFillet","BLEND_FACE",FACE,{"disambiguationData":[OSD([subQ0,sQuery(id+"F0.wireOp",EDGE,"E0.right")])]})]});}
            chamfer(context, id + "F12", {"entities" : qUnion([Q0, Q1, Q2]), "width" : 5.08 * mm, "tangentPropagation" : true});
        }
        {
            var Q0;
            {var subQ0=sQuery(id+"F0.wireOp",EDGE,"E0.top");var subQ1=sQuery(id+"F3.wireOp",EDGE,"E3.2");var subQ2=sQuery(id+"F3.wireOp",EDGE,"E3.1");Q0=makeQuery(id+"F7.opFillet","BLEND_EDGE",EDGE,{"blendedFrom":[makeQuery(id+"F4.boolean.opBoolean","SPLIT",EDGE,{"disambiguationData":[TD([makeQuery(id+"F4.opExtrude","SWEPT_FACE",FACE,{"disambiguationData":[OSD([subQ2])]})])],"derivedFrom":makeQuery(id+"F4.opExtrude","CAP_EDGE",EDGE,{"disambiguationData":[OSD([subQ1])],"isStart":true})}),makeQuery(id+"F6.opFillet","BLEND_FACE",FACE,{"disambiguationData":[OSD([subQ0,sQuery(id+"F0.wireOp",EDGE,"E0.right")])]})],"blendedInto":[makeQuery(id+"F6.opFillet","BLEND_FACE",FACE,{"disambiguationData":[OSD([subQ0,sQuery(id+"F0.wireOp",EDGE,"E0.right")])]})]});}
            var Q1;
            {var subQ0=sQuery(id+"F0.wireOp",EDGE,"E0.top");var subQ1=sQuery(id+"F3.wireOp",EDGE,"E3.1");var subQ2=sQuery(id+"F3.wireOp",EDGE,"E3.2");Q1=makeQuery(id+"F6.opFillet","BLEND_EDGE",EDGE,{"blendedFrom":[makeQuery(id+"F2.opRevolve","SWEPT_EDGE",EDGE,{"disambiguationData":[OSD([subQ0,sQuery(id+"F0.wireOp",EDGE,"E0.right")])]}),makeQuery(id+"F4.boolean.opBoolean","SPLIT",FACE,{"disambiguationData":[TD([makeQuery(id+"F2.opRevolve","SWEPT_FACE",FACE,{"disambiguationData":[OSD([subQ0])]}),makeQuery(id+"F4.opExtrude","SWEPT_FACE",FACE,{"disambiguationData":[OSD([subQ1])]}),makeQuery(id+"F4.opExtrude","SWEPT_FACE",FACE,{"disambiguationData":[OSD([subQ2])]})])],"derivedFrom":makeQuery(id+"F4.opExtrude","CAP_FACE",FACE,{"disambiguationData":[OSD([sQuery(id+"F3.wireOp",EDGE,"E3.0"),subQ1,subQ2,sQuery(id+"F3.wireOp",EDGE,"E3.3"),sQuery(id+"F3.wireOp",EDGE,"E3.4"),sQuery(id+"F3.wireOp",EDGE,"E3.5")])],"isStart":true})})],"blendedInto":[makeQuery(id+"F4.boolean.opBoolean","SPLIT",FACE,{"disambiguationData":[TD([makeQuery(id+"F2.opRevolve","SWEPT_FACE",FACE,{"disambiguationData":[OSD([subQ0])]}),makeQuery(id+"F4.opExtrude","SWEPT_FACE",FACE,{"disambiguationData":[OSD([subQ1])]}),makeQuery(id+"F4.opExtrude","SWEPT_FACE",FACE,{"disambiguationData":[OSD([subQ2])]})])],"derivedFrom":makeQuery(id+"F4.opExtrude","CAP_FACE",FACE,{"disambiguationData":[OSD([sQuery(id+"F3.wireOp",EDGE,"E3.0"),subQ1,subQ2,sQuery(id+"F3.wireOp",EDGE,"E3.3"),sQuery(id+"F3.wireOp",EDGE,"E3.4"),sQuery(id+"F3.wireOp",EDGE,"E3.5")])],"isStart":true})})]});}
            var Q2;
            {var subQ0=sQuery(id+"F0.wireOp",EDGE,"E0.top");var subQ1=sQuery(id+"F3.wireOp",EDGE,"E3.2");var subQ2=sQuery(id+"F3.wireOp",EDGE,"E3.1");Q2=makeQuery(id+"F7.opFillet","BLEND_EDGE",EDGE,{"blendedFrom":[makeQuery(id+"F4.boolean.opBoolean","SPLIT",EDGE,{"disambiguationData":[TD([makeQuery(id+"F4.opExtrude","SWEPT_FACE",FACE,{"disambiguationData":[OSD([subQ1])]})])],"derivedFrom":makeQuery(id+"F4.opExtrude","CAP_EDGE",EDGE,{"disambiguationData":[OSD([subQ2])],"isStart":true})}),makeQuery(id+"F6.opFillet","BLEND_FACE",FACE,{"disambiguationData":[OSD([subQ0,sQuery(id+"F0.wireOp",EDGE,"E0.right")])]})],"blendedInto":[makeQuery(id+"F6.opFillet","BLEND_FACE",FACE,{"disambiguationData":[OSD([subQ0,sQuery(id+"F0.wireOp",EDGE,"E0.right")])]})]});}
            chamfer(context, id + "F13", {"entities" : qUnion([Q0, Q1, Q2]), "width" : 5.08 * mm, "tangentPropagation" : true});
        }
        {
            var Q0;
            {var subQ0=sQuery(id+"F3.wireOp",EDGE,"E3.2");Q0=makeQuery(id+"F5.opFillet","BLEND_EDGE",EDGE,{"blendedFrom":[makeQuery(id+"F4.opExtrude","CAP_EDGE",EDGE,{"disambiguationData":[OSD([subQ0])],"isStart":false}),makeQuery(id+"F4.boolean.opBoolean","SPLIT",FACE,{"disambiguationData":[TD([makeQuery(id+"F4.opExtrude","CAP_FACE",FACE,{"disambiguationData":[OSD([sQuery(id+"F3.wireOp",EDGE,"E3.0"),sQuery(id+"F3.wireOp",EDGE,"E3.1"),subQ0,sQuery(id+"F3.wireOp",EDGE,"E3.3"),sQuery(id+"F3.wireOp",EDGE,"E3.4"),sQuery(id+"F3.wireOp",EDGE,"E3.5")])],"isStart":false})])],"derivedFrom":makeQuery(id+"F2.opRevolve","SWEPT_FACE",FACE,{"disambiguationData":[OSD([sQuery(id+"F0.wireOp",EDGE,"E1")])]})})],"blendedInto":[makeQuery(id+"F4.boolean.opBoolean","SPLIT",FACE,{"disambiguationData":[TD([makeQuery(id+"F4.opExtrude","CAP_FACE",FACE,{"disambiguationData":[OSD([sQuery(id+"F3.wireOp",EDGE,"E3.0"),sQuery(id+"F3.wireOp",EDGE,"E3.1"),subQ0,sQuery(id+"F3.wireOp",EDGE,"E3.3"),sQuery(id+"F3.wireOp",EDGE,"E3.4"),sQuery(id+"F3.wireOp",EDGE,"E3.5")])],"isStart":false})])],"derivedFrom":makeQuery(id+"F2.opRevolve","SWEPT_FACE",FACE,{"disambiguationData":[OSD([sQuery(id+"F0.wireOp",EDGE,"E1")])]})})]});}
            var Q1;
            Q1=makeQuery(id+"F4.boolean.opBoolean","INTERSECT",EDGE,{"derivedFrom":[makeQuery(id+"F2.opRevolve","SWEPT_FACE",FACE,{"disambiguationData":[OSD([sQuery(id+"F0.wireOp",EDGE,"E1")])]}),makeQuery(id+"F4.opExtrude","CAP_FACE",FACE,{"disambiguationData":[OSD([sQuery(id+"F3.wireOp",EDGE,"E3.0"),sQuery(id+"F3.wireOp",EDGE,"E3.1"),sQuery(id+"F3.wireOp",EDGE,"E3.2"),sQuery(id+"F3.wireOp",EDGE,"E3.3"),sQuery(id+"F3.wireOp",EDGE,"E3.4"),sQuery(id+"F3.wireOp",EDGE,"E3.5")])],"isStart":false})]});
            var Q2;
            Q2=makeQuery(id+"F4.boolean.opBoolean","INTERSECT",EDGE,{"derivedFrom":[makeQuery(id+"F2.opRevolve","SWEPT_FACE",FACE,{"disambiguationData":[OSD([sQuery(id+"F0.wireOp",EDGE,"E1")])]}),makeQuery(id+"F4.opExtrude","CAP_FACE",FACE,{"disambiguationData":[OSD([sQuery(id+"F3.wireOp",EDGE,"E3.0"),sQuery(id+"F3.wireOp",EDGE,"E3.1"),sQuery(id+"F3.wireOp",EDGE,"E3.2"),sQuery(id+"F3.wireOp",EDGE,"E3.3"),sQuery(id+"F3.wireOp",EDGE,"E3.4"),sQuery(id+"F3.wireOp",EDGE,"E3.5")])],"isStart":false})]});
            var Q3;
            {var subQ0=sQuery(id+"F3.wireOp",EDGE,"E3.5");Q3=makeQuery(id+"F5.opFillet","BLEND_EDGE",EDGE,{"blendedFrom":[makeQuery(id+"F4.opExtrude","CAP_EDGE",EDGE,{"disambiguationData":[OSD([subQ0])],"isStart":false}),makeQuery(id+"F4.boolean.opBoolean","SPLIT",FACE,{"disambiguationData":[TD([makeQuery(id+"F4.opExtrude","CAP_FACE",FACE,{"disambiguationData":[OSD([sQuery(id+"F3.wireOp",EDGE,"E3.0"),sQuery(id+"F3.wireOp",EDGE,"E3.1"),sQuery(id+"F3.wireOp",EDGE,"E3.2"),sQuery(id+"F3.wireOp",EDGE,"E3.3"),sQuery(id+"F3.wireOp",EDGE,"E3.4"),subQ0])],"isStart":false})])],"derivedFrom":makeQuery(id+"F2.opRevolve","SWEPT_FACE",FACE,{"disambiguationData":[OSD([sQuery(id+"F0.wireOp",EDGE,"E1")])]})})],"blendedInto":[makeQuery(id+"F4.boolean.opBoolean","SPLIT",FACE,{"disambiguationData":[TD([makeQuery(id+"F4.opExtrude","CAP_FACE",FACE,{"disambiguationData":[OSD([sQuery(id+"F3.wireOp",EDGE,"E3.0"),sQuery(id+"F3.wireOp",EDGE,"E3.1"),sQuery(id+"F3.wireOp",EDGE,"E3.2"),sQuery(id+"F3.wireOp",EDGE,"E3.3"),sQuery(id+"F3.wireOp",EDGE,"E3.4"),subQ0])],"isStart":false})])],"derivedFrom":makeQuery(id+"F2.opRevolve","SWEPT_FACE",FACE,{"disambiguationData":[OSD([sQuery(id+"F0.wireOp",EDGE,"E1")])]})})]});}
            chamfer(context, id + "F14", {"entities" : qUnion([Q0, Q1, Q2, Q3]), "width" : 1.27 * mm, "tangentPropagation" : true});
        }
        {
            var Q0;
            Q0=qCreatedBy(makeId("Front.planeOp"),FACE);
            var sketch = newSketch(context, id + "F15", { "sketchPlane" : qUnion([Q0])});
            skCircle(sketch, "E4", {"center": v(0, 0) * mm, "radius": 0.64 * mm});
            skSolve(sketch);
        }
        {
            var Q0;
            Q0=sQuery(id+"F15.wireOp",EDGE,"E4");
            extrude(context, id + "F16", {"bodyType" : ToolBodyType.SURFACE, "surfaceEntities" : qUnion([Q0]), "endBound" : BoundingType.UP_TO_NEXT, "depth" : 25.4 * mm, "offsetDistance" : 25.4 * mm});
        }
    });
